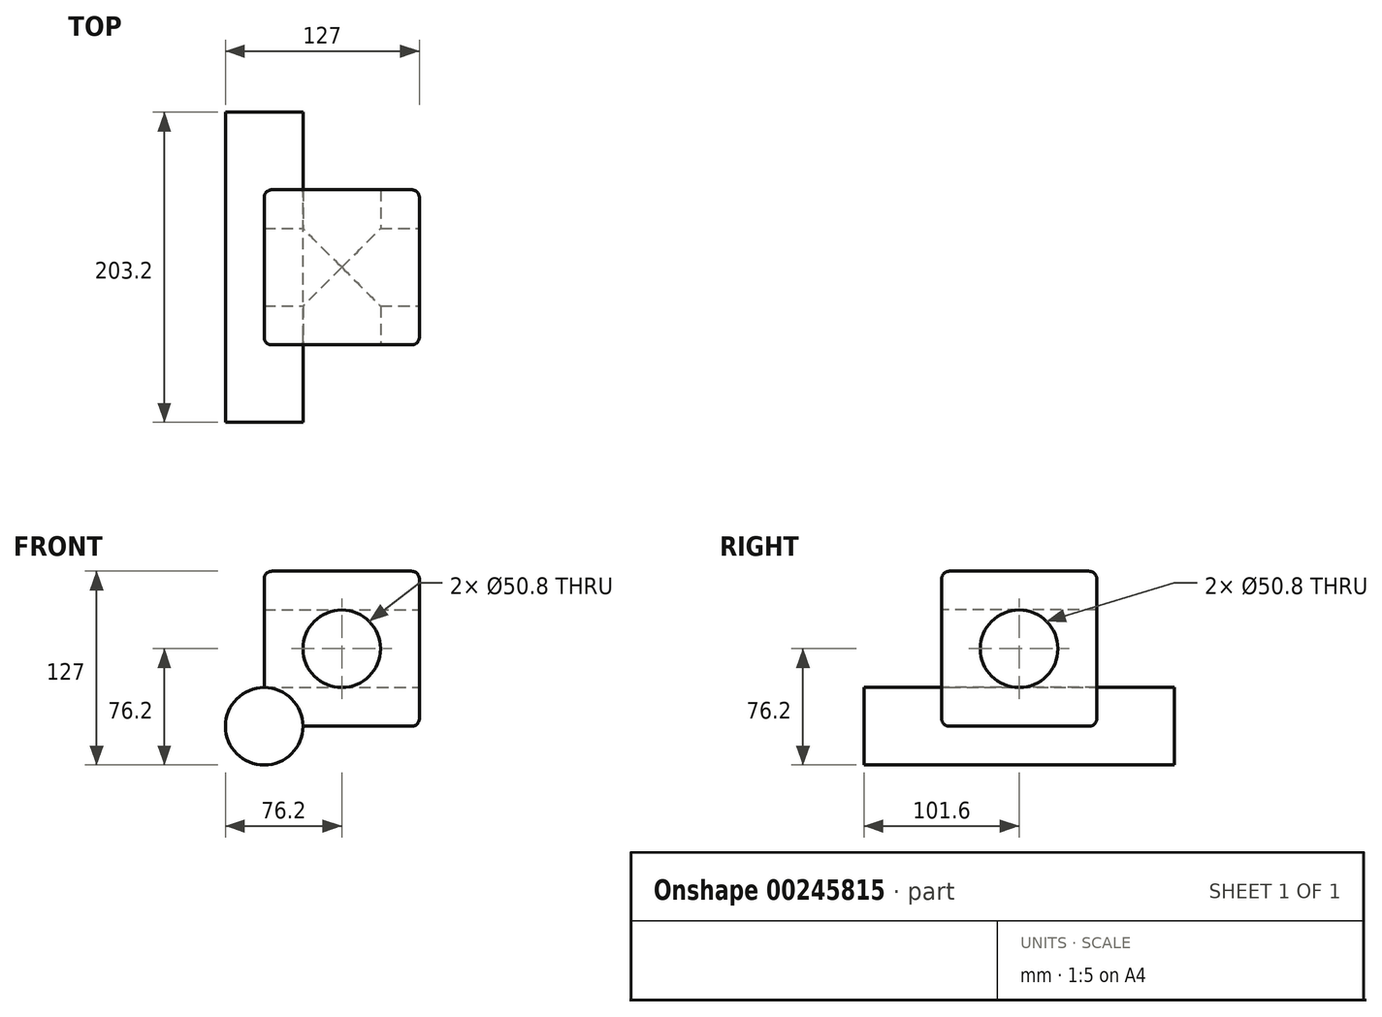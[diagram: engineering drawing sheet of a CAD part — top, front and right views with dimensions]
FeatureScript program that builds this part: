
annotation { "Feature Type Name" : "Feature", "Feature Type Description" : "" }
export const myFeature = defineFeature(function(context is Context, id is Id, definition is map)
    precondition{}
    {
        {
            var Q0;
            Q0=qCreatedBy(makeId("Front.planeOp"),FACE);
            var sketch = newSketch(context, id + "F0", { "sketchPlane" : qUnion([Q0])});
            skLineSegment(sketch, "E0", {"start": v(0, 0) * mm, "end": v(101.6, 0) * mm});
            skLineSegment(sketch, "E1", {"start": v(101.6, 0) * mm, "end": v(101.6, 101.6) * mm});
            skLineSegment(sketch, "E2", {"start": v(101.6, 101.6) * mm, "end": v(0, 101.6) * mm});
            skLineSegment(sketch, "E3", {"start": v(0, 101.6) * mm, "end": v(0, 0) * mm});
            skSolve(sketch);
        }
        {
            var Q0;
            Q0=makeQuery(id+"F0.imprint","IMPRINT",FACE,{"disambiguationData":[TD([[makeQuery(id+"F0.imprint","IMPRINT",EDGE,{"derivedFrom":sQuery(id+"F0.wireOp",EDGE,"E0")}),1.0]])]});
            extrude(context, id + "F1", {"entities" : qUnion([Q0]), "depth" : 101.6 * mm});
        }
        {
            var Q0;
            Q0=makeQuery(id+"F1.opExtrude","CAP_FACE",FACE,{"disambiguationData":[OSD([sQuery(id+"F0.wireOp",EDGE,"E0"),sQuery(id+"F0.wireOp",EDGE,"E1"),sQuery(id+"F0.wireOp",EDGE,"E2"),sQuery(id+"F0.wireOp",EDGE,"E3")])],"isStart":false});
            var sketch = newSketch(context, id + "F2", { "sketchPlane" : qUnion([Q0])});
            skPoint(sketch, "E4.center.orphan", {"position": v(50.8, 50.8) * mm});
            skCircle(sketch, "E5", {"center": v(50.8, 50.8) * mm, "radius": 25.4 * mm});
            skPoint(sketch, "E6.orphan", {"position": v(50.8, 101.6) * mm});
            skPoint(sketch, "E7.end.orphan", {"position": v(50.8, 0) * mm});
            skSolve(sketch);
        }
        {
            var Q0;
            Q0 = qSketchRegion(id + "F2", true);
            extrude(context, id + "F3", {"entities" : qUnion([Q0]), "operationType" : NewBodyOperationType.REMOVE, "oppositeDirection" : true, "depth" : 101.6 * mm});
        }
        {
            var Q0;
            Q0=makeQuery(id+"F1.opExtrude","SWEPT_FACE",FACE,{"disambiguationData":[OSD([sQuery(id+"F0.wireOp",EDGE,"E1")])]});
            var sketch = newSketch(context, id + "F4", { "sketchPlane" : qUnion([Q0])});
            skCircle(sketch, "E8", {"center": v(-50.8, 50.8) * mm, "radius": 25.4 * mm});
            skPoint(sketch, "E9.orphan", {"position": v(-50.8, 101.6) * mm});
            skPoint(sketch, "E10.end.orphan", {"position": v(-50.8, 0) * mm});
            skSolve(sketch);
        }
        {
            var Q0;
            Q0=makeQuery(id+"F4.imprint","IMPRINT",FACE,{"disambiguationData":[TD([[makeQuery(id+"F4.imprint","IMPRINT",EDGE,{"derivedFrom":sQuery(id+"F4.wireOp",EDGE,"E8")}),1.0]])]});
            extrude(context, id + "F5", {"entities" : qUnion([Q0]), "operationType" : NewBodyOperationType.REMOVE, "oppositeDirection" : true, "depth" : 101.6 * mm});
        }
        {
            var Q0;
            Q0=makeQuery(id+"F1.opExtrude","CAP_EDGE",EDGE,{"disambiguationData":[OSD([sQuery(id+"F0.wireOp",EDGE,"E2")])],"isStart":false});
            var Q1;
            Q1=makeQuery(id+"F1.opExtrude","SWEPT_EDGE",EDGE,{"disambiguationData":[OSD([sQuery(id+"F0.wireOp",EDGE,"E1"),sQuery(id+"F0.wireOp",EDGE,"E2")])]});
            var Q2;
            Q2=makeQuery(id+"F1.opExtrude","CAP_EDGE",EDGE,{"disambiguationData":[OSD([sQuery(id+"F0.wireOp",EDGE,"E1")])],"isStart":false});
            var Q3;
            Q3=makeQuery(id+"F1.opExtrude","CAP_EDGE",EDGE,{"disambiguationData":[OSD([sQuery(id+"F0.wireOp",EDGE,"E0")])],"isStart":false});
            var Q4;
            Q4=makeQuery(id+"F1.opExtrude","SWEPT_EDGE",EDGE,{"disambiguationData":[OSD([sQuery(id+"F0.wireOp",EDGE,"E0"),sQuery(id+"F0.wireOp",EDGE,"E1")])]});
            var Q5;
            Q5=makeQuery(id+"F1.opExtrude","CAP_EDGE",EDGE,{"disambiguationData":[OSD([sQuery(id+"F0.wireOp",EDGE,"E1")])],"isStart":true});
            var Q6;
            Q6=makeQuery(id+"F1.opExtrude","SWEPT_EDGE",EDGE,{"disambiguationData":[OSD([sQuery(id+"F0.wireOp",EDGE,"E2"),sQuery(id+"F0.wireOp",EDGE,"E3")])]});
            var Q7;
            Q7=makeQuery(id+"F1.opExtrude","CAP_EDGE",EDGE,{"disambiguationData":[OSD([sQuery(id+"F0.wireOp",EDGE,"E2")])],"isStart":true});
            var Q8;
            Q8=makeQuery(id+"F1.opExtrude","SWEPT_EDGE",EDGE,{"disambiguationData":[OSD([sQuery(id+"F0.wireOp",EDGE,"E0"),sQuery(id+"F0.wireOp",EDGE,"E3")])]});
            var Q9;
            Q9=makeQuery(id+"F1.opExtrude","CAP_EDGE",EDGE,{"disambiguationData":[OSD([sQuery(id+"F0.wireOp",EDGE,"E0")])],"isStart":true});
            var Q10;
            Q10=makeQuery(id+"F1.opExtrude","CAP_EDGE",EDGE,{"disambiguationData":[OSD([sQuery(id+"F0.wireOp",EDGE,"E3")])],"isStart":false});
            var Q11;
            Q11=makeQuery(id+"F1.opExtrude","CAP_EDGE",EDGE,{"disambiguationData":[OSD([sQuery(id+"F0.wireOp",EDGE,"E3")])],"isStart":true});
            fillet(context, id + "F6", {"entities" : qUnion([Q0, Q1, Q2, Q3, Q4, Q5, Q6, Q7, Q8, Q9, Q10, Q11]), "radius" : 5.08 * mm, "tangentPropagation" : true, "allowEdgeOverflow" : false});
        }
        {
            var Q0;
            Q0=qCreatedBy(makeId("Front.planeOp"),FACE);
            cPlane(context, id + "F7", {"entities" : qUnion([Q0]), "cplaneType" : CPlaneType.OFFSET, "offset" : 101.6 * mm, "width" : 152.4 * mm, "height" : 152.4 * mm});
        }
        {
            var Q0;
            Q0=qCreatedBy(id+"F7.planeOp",FACE);
            var sketch = newSketch(context, id + "F8", { "sketchPlane" : qUnion([Q0])});
            skCircle(sketch, "E11", {"center": v(0, 0) * mm, "radius": 25.4 * mm});
            skSolve(sketch);
        }
        {
            var Q0;
            Q0=makeQuery(id+"F8.imprint","IMPRINT",FACE,{"disambiguationData":[TD([[makeQuery(id+"F8.imprint","IMPRINT",EDGE,{"derivedFrom":sQuery(id+"F8.wireOp",EDGE,"E11")}),1.0]])]});
            extrude(context, id + "F9", {"entities" : qUnion([Q0]), "operationType" : NewBodyOperationType.ADD, "depth" : 50.8 * mm, "hasSecondDirection" : true, "secondDirectionOppositeDirection" : true, "secondDirectionDepth" : 152.4 * mm});
        }
    });
